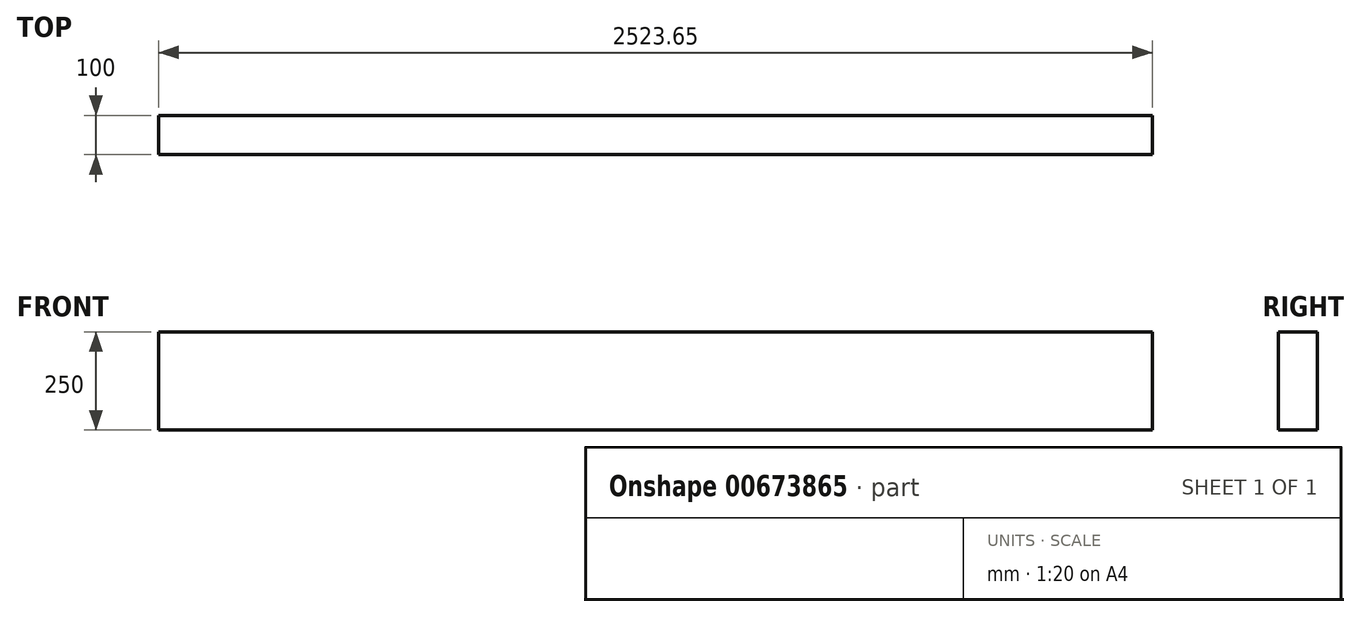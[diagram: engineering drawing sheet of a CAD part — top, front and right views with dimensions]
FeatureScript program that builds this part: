
annotation { "Feature Type Name" : "Feature", "Feature Type Description" : "" }
export const myFeature = defineFeature(function(context is Context, id is Id, definition is map)
    precondition{}
    {
        {
            var Q0;
            Q0=qCreatedBy(makeId("Front.planeOp"),FACE);
            var sketch = newSketch(context, id + "F0", { "sketchPlane" : qUnion([Q0])});
            skLineSegment(sketch, "E0.bottom", {"start": v(-1255.76, 139.28) * mm, "end": v(1267.9, 139.28) * mm});
            skLineSegment(sketch, "E0.top", {"start": v(-1255.76, -110.72) * mm, "end": v(1267.9, -110.72) * mm});
            skLineSegment(sketch, "E0.left", {"start": v(-1255.76, 139.28) * mm, "end": v(-1255.76, -110.72) * mm});
            skLineSegment(sketch, "E1.trimOffspring", {"start": v(1267.9, -110.72) * mm, "end": v(1267.9, 139.28) * mm});
            skSolve(sketch);
        }
        {
            var Q0;
            Q0 = qSketchRegion(id + "F0", true);
            extrude(context, id + "F1", {"entities" : qUnion([Q0]), "depth" : 100 * mm, "offsetDistance" : 25 * mm});
        }
    });
